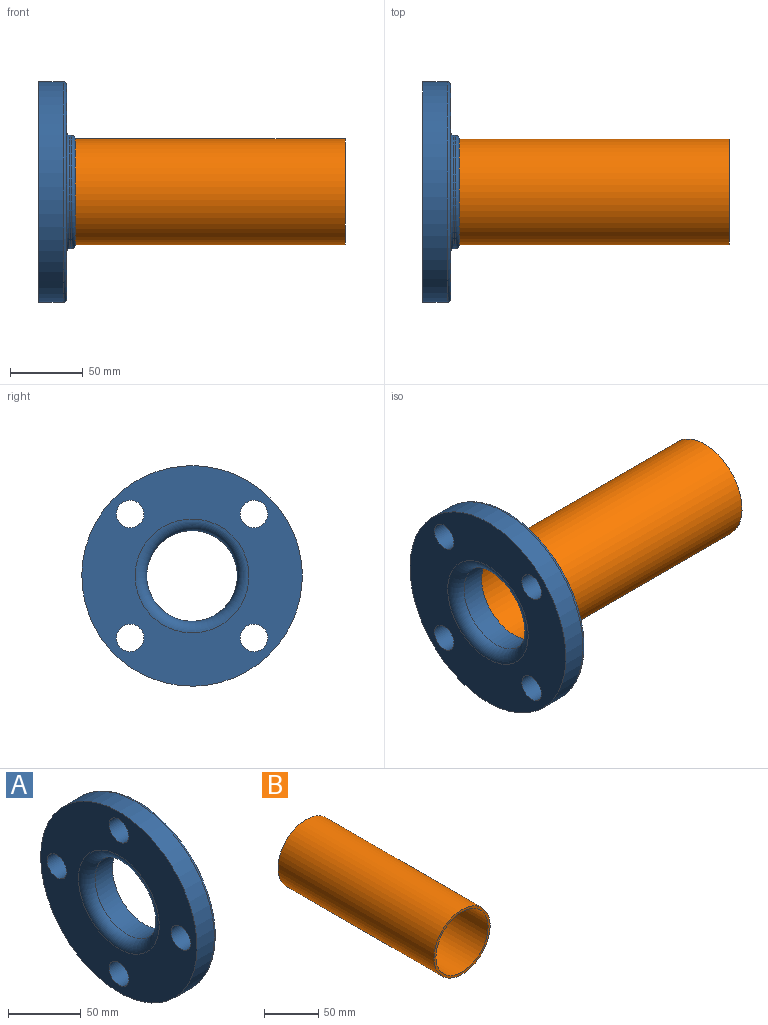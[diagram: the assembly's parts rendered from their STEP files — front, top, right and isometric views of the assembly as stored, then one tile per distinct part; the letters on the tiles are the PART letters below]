
ASSEMBLY  parts=2 mates=1
PART A: 14 faces, bbox 25x164.5x164.5 mm
  f0: cylinder r=31.25mm len=62.5mm, axis (1,0,0), area 3337.9mm2, adj f2,f13
  f1: plane 152x152mm, normal (-1,0,0), area 12171.9mm2, adj f8,f9,f10,f11,f12,f13
  f2: plane 73.31x73.31mm, normal (1,0,0), area 1153.4mm2, adj f0,f3
  f3: torus R=36.66mm, axis (-1,0,0), area 882.4mm2, adj f2,f4
  f4: cylinder r=39mm len=78mm, axis (-1,0,0), area 297.2mm2, adj f3,f5
  f5: torus R=41.34mm, axis (-1,0,0), area 921.8mm2, adj f4,f6
  f6: plane 147.31x147.31mm, normal (1,0,0), area 10539.9mm2, adj f5,f7,f9,f10,f11,f12
  f7: torus R=73.66mm, axis (-1,0,0), area 1738.3mm2, adj f6,f8
  f8: cylinder r=76mm len=152mm, axis (-1,0,0), area 8001.5mm2, adj f1,f7
  f9: cylinder r=9.5mm len=19.1mm, axis (1,0,0), area 1140.1mm2, adj f1,f6
  f10: cylinder r=9.5mm len=19.1mm, axis (1,0,0), area 1140.1mm2, adj f1,f6
  f11: cylinder r=9.5mm len=19.1mm, axis (1,0,0), area 1140.1mm2, adj f1,f6
  f12: cylinder r=9.5mm len=19.1mm, axis (1,0,0), area 1140.1mm2, adj f1,f6
  f13: torus R=39.25mm, axis (-1,0,0), area 2696.9mm2, adj f0,f1
PART B: 4 faces, bbox 73x203.2x73 mm
  f0: plane 73.03x73.03mm, normal (0,-1,0), area 562.4mm2, adj f2,f3
  f1: plane 73.03x73.03mm, normal (0,1,0), area 562.4mm2, adj f2,f3
  f2: cylinder r=36.51mm len=203.2mm, axis (0,1,0), area 46617.1mm2, adj f0,f1
  f3: cylinder r=33.97mm len=203.2mm, axis (0,1,0), area 43374.2mm2, adj f0,f1
PLACE A rot(axis=(1,0,0),45deg) t=(-84.2,0,0)mm
PLACE B rot(axis=(0.58,0.58,-0.58),120deg) t=(89.05,0,-4637.67)mm fixed
MATE fastened A.f0 <-> B.f2  axis (1,0,0) through (-76.2,0,0)mm
